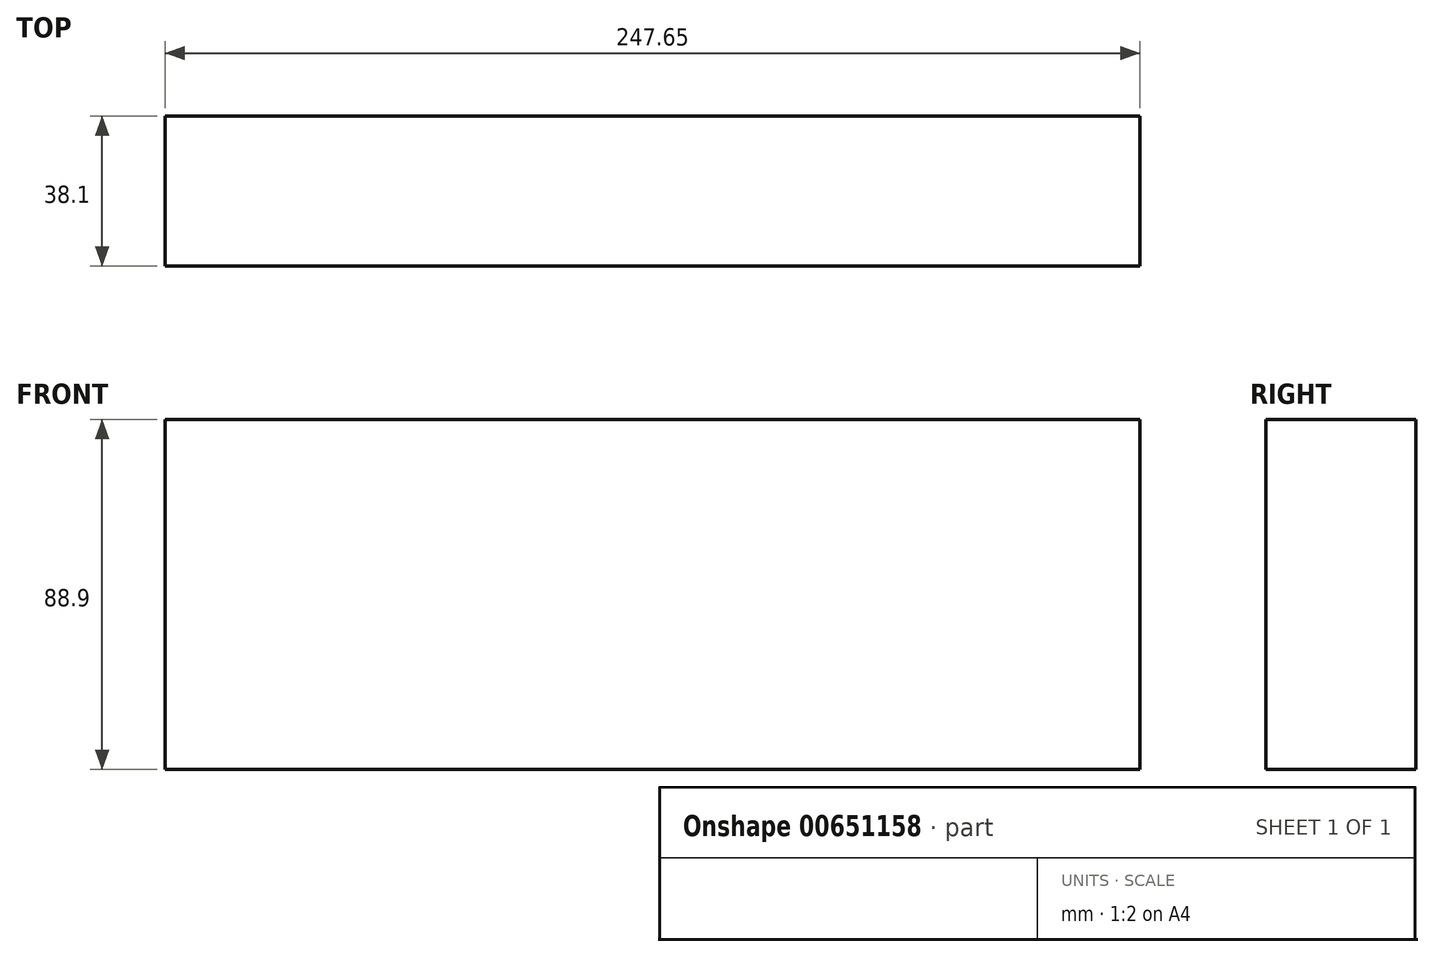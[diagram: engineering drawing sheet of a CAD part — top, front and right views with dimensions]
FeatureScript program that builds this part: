
annotation { "Feature Type Name" : "Feature", "Feature Type Description" : "" }
export const myFeature = defineFeature(function(context is Context, id is Id, definition is map)
    precondition{}
    {
        {
            var Q0;
            Q0=qCreatedBy(makeId("Right.planeOp"),FACE);
            var sketch = newSketch(context, id + "F0", { "sketchPlane" : qUnion([Q0])});
            skLineSegment(sketch, "E0.bottom", {"start": v(19.05, 44.45) * mm, "end": v(-19.05, 44.45) * mm});
            skLineSegment(sketch, "E0.top", {"start": v(19.05, -44.45) * mm, "end": v(-19.05, -44.45) * mm});
            skLineSegment(sketch, "E0.left", {"start": v(19.05, 44.45) * mm, "end": v(19.05, -44.45) * mm});
            skLineSegment(sketch, "E0.right", {"start": v(-19.05, 44.45) * mm, "end": v(-19.05, -44.45) * mm});
            skPoint(sketch, "E0.middle", {"position": v(0, 0) * mm});
            skSolve(sketch);
        }
        {
            var Q0;
            Q0=makeQuery(id+"F0.imprint","IMPRINT",FACE,{"disambiguationData":[TD([[makeQuery(id+"F0.imprint","IMPRINT",EDGE,{"derivedFrom":sQuery(id+"F0.wireOp",EDGE,"E0.bottom")}),1.0]])]});
            extrude(context, id + "F1", {"entities" : qUnion([Q0]), "depth" : 247.65 * mm, "offsetDistance" : 25.4 * mm});
        }
    });
